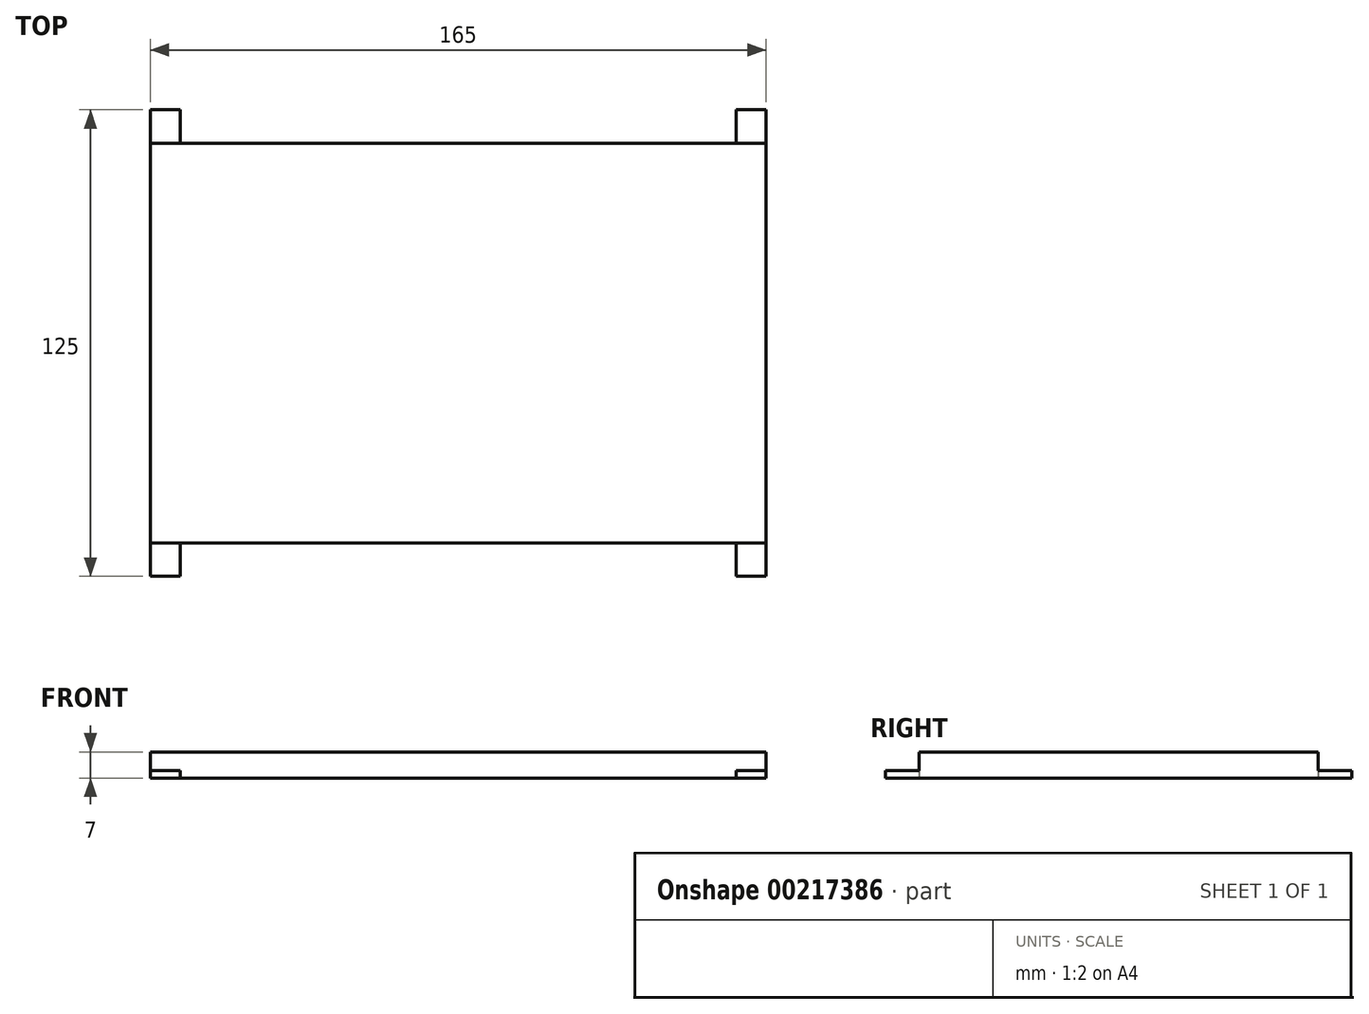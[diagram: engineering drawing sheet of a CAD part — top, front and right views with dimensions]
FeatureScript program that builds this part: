
annotation { "Feature Type Name" : "Feature", "Feature Type Description" : "" }
export const myFeature = defineFeature(function(context is Context, id is Id, definition is map)
    precondition{}
    {
        {
            var Q0;
            Q0=qCreatedBy(makeId("Top.planeOp"),FACE);
            var sketch = newSketch(context, id + "F0", { "sketchPlane" : qUnion([Q0])});
            skLineSegment(sketch, "E0.bottom", {"start": v(82.5, 62.5) * mm, "end": v(74.5, 62.5) * mm});
            skLineSegment(sketch, "E0.top", {"start": v(82.5, -62.5) * mm, "end": v(74.5, -62.5) * mm});
            skLineSegment(sketch, "E0.left", {"start": v(82.5, 62.5) * mm, "end": v(82.5, -62.5) * mm});
            skLineSegment(sketch, "E0.right", {"start": v(-82.5, 62.5) * mm, "end": v(-82.5, -62.5) * mm});
            skPoint(sketch, "E0.middle", {"position": v(0, 0) * mm});
            skLineSegment(sketch, "E1.bottom", {"start": v(74.5, -53.5) * mm, "end": v(-74.5, -53.5) * mm});
            skLineSegment(sketch, "E1.top", {"start": v(74.5, 53.5) * mm, "end": v(-74.5, 53.5) * mm});
            skLineSegment(sketch, "E1.left", {"start": v(82.5, -53.5) * mm, "end": v(82.5, 53.5) * mm});
            skLineSegment(sketch, "E1.right", {"start": v(-82.5, -53.5) * mm, "end": v(-82.5, 53.5) * mm});
            skLineSegment(sketch, "E2.left", {"start": v(74.5, 62.5) * mm, "end": v(74.5, 53.5) * mm});
            skLineSegment(sketch, "E2.right", {"start": v(-74.5, 62.5) * mm, "end": v(-74.5, 53.5) * mm});
            skLineSegment(sketch, "E3.trimOffspring", {"start": v(-74.5, 62.5) * mm, "end": v(-82.5, 62.5) * mm});
            skLineSegment(sketch, "E4.trimOffspring", {"start": v(-74.5, -62.5) * mm, "end": v(-82.5, -62.5) * mm});
            skLineSegment(sketch, "E5.trimOffspring", {"start": v(74.5, -53.5) * mm, "end": v(74.5, -62.5) * mm});
            skLineSegment(sketch, "E6.trimOffspring", {"start": v(-74.5, -53.5) * mm, "end": v(-74.5, -62.5) * mm});
            skSolve(sketch);
        }
        {
            var Q0;
            {var subQ0=sQuery(id+"F0.wireOp",EDGE,"E0.bottom");Q0=makeQuery(id+"F0.imprint","IMPRINT",FACE,{"disambiguationData":[TD([[makeQuery(id+"F0.imprint","IMPRINT",EDGE,{"derivedFrom":subQ0}),1.0]])]});}
            extrude(context, id + "F1", {"entities" : qUnion([Q0]), "depth" : 2 * mm});
        }
        {
            var Q0;
            Q0=makeQuery(id+"F1.opExtrude","CAP_FACE",FACE,{"disambiguationData":[OSD([sQuery(id+"F0.wireOp",EDGE,"E0.bottom"),sQuery(id+"F0.wireOp",EDGE,"E0.top"),sQuery(id+"F0.wireOp",EDGE,"E0.left"),sQuery(id+"F0.wireOp",EDGE,"E0.right"),sQuery(id+"F0.wireOp",EDGE,"E1.bottom"),sQuery(id+"F0.wireOp",EDGE,"E1.top"),sQuery(id+"F0.wireOp",EDGE,"E1.left"),sQuery(id+"F0.wireOp",EDGE,"E1.right"),sQuery(id+"F0.wireOp",EDGE,"E2.left"),sQuery(id+"F0.wireOp",EDGE,"E2.right"),sQuery(id+"F0.wireOp",EDGE,"E3.trimOffspring"),sQuery(id+"F0.wireOp",EDGE,"E4.trimOffspring"),sQuery(id+"F0.wireOp",EDGE,"E5.trimOffspring"),sQuery(id+"F0.wireOp",EDGE,"E6.trimOffspring")])],"isStart":false});
            var sketch = newSketch(context, id + "F2", { "sketchPlane" : qUnion([Q0])});
            skLineSegment(sketch, "E7.bottom", {"start": v(82.5, 53.5) * mm, "end": v(-82.5, 53.5) * mm});
            skLineSegment(sketch, "E7.top", {"start": v(82.5, -53.5) * mm, "end": v(-82.5, -53.5) * mm});
            skLineSegment(sketch, "E7.left", {"start": v(82.5, 53.5) * mm, "end": v(82.5, -53.5) * mm});
            skLineSegment(sketch, "E7.right", {"start": v(-82.5, 53.5) * mm, "end": v(-82.5, -53.5) * mm});
            skPoint(sketch, "E7.middle", {"position": v(0, 0) * mm});
            skSolve(sketch);
        }
        {
            var Q0;
            {var subQ2=sQuery(id+"F2.wireOp",EDGE,"E7.left");Q0=makeQuery(id+"F2.imprint","IMPRINT",FACE,{"disambiguationData":[TD([[makeQuery(id+"F2.imprint","IMPRINT",EDGE,{"derivedFrom":subQ2}),-1.0]])]});}
            extrude(context, id + "F3", {"entities" : qUnion([Q0]), "operationType" : NewBodyOperationType.ADD, "depth" : 5 * mm});
        }
    });
